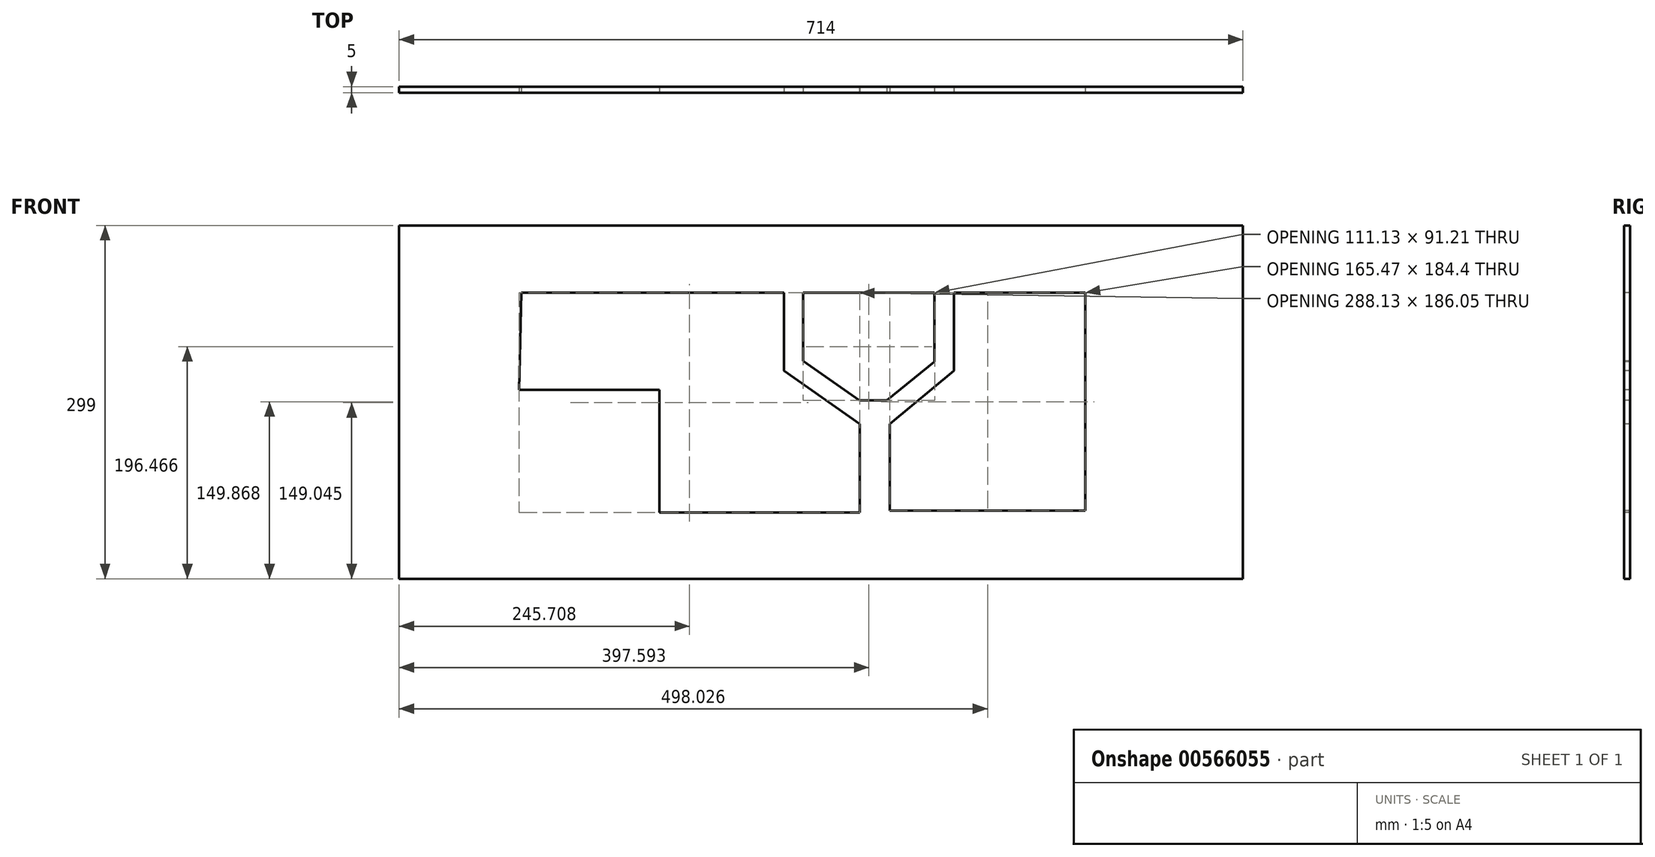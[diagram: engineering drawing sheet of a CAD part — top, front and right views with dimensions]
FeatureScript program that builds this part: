
annotation { "Feature Type Name" : "Feature", "Feature Type Description" : "" }
export const myFeature = defineFeature(function(context is Context, id is Id, definition is map)
    precondition{}
    {
        {
            var Q0;
            Q0=qCreatedBy(makeId("Top.planeOp"),FACE);
            var sketch = newSketch(context, id + "F0", { "sketchPlane" : qUnion([Q0])});
            skLineSegment(sketch, "E0.bottom", {"start": v(-666.68, 27.8) * mm, "end": v(47.32, 27.8) * mm});
            skLineSegment(sketch, "E0.top", {"start": v(-666.68, 22.8) * mm, "end": v(47.32, 22.8) * mm});
            skLineSegment(sketch, "E0.left", {"start": v(-666.68, 27.8) * mm, "end": v(-666.68, 22.8) * mm});
            skLineSegment(sketch, "E0.right", {"start": v(47.32, 27.8) * mm, "end": v(47.32, 22.8) * mm});
            skSolve(sketch);
        }
        {
            var Q0;
            Q0 = qSketchRegion(id + "F0", true);
            extrude(context, id + "F1", {"entities" : qUnion([Q0]), "depth" : 299 * mm, "offsetDistance" : 25 * mm});
        }
        {
            var Q0;
            Q0=makeQuery(id+"F1.opExtrude","SWEPT_FACE",FACE,{"disambiguationData":[OSD([sQuery(id+"F0.wireOp",EDGE,"E0.top")])]});
            var sketch = newSketch(context, id + "F2", { "sketchPlane" : qUnion([Q0])});
            skLineSegment(sketch, "E1", {"start": v(-563.39, 242.07) * mm, "end": v(-341.12, 242.07) * mm});
            skLineSegment(sketch, "E2", {"start": v(-341.12, 242.07) * mm, "end": v(-341.12, 176.21) * mm});
            skLineSegment(sketch, "E3", {"start": v(-341.12, 176.21) * mm, "end": v(-276.9, 130.93) * mm});
            skLineSegment(sketch, "E4", {"start": v(-276.9, 130.93) * mm, "end": v(-276.9, 56.02) * mm});
            skLineSegment(sketch, "E5", {"start": v(-276.9, 56.02) * mm, "end": v(-446.5, 56.02) * mm});
            skLineSegment(sketch, "E6", {"start": v(-446.5, 56.02) * mm, "end": v(-446.5, 159.75) * mm});
            skLineSegment(sketch, "E7", {"start": v(-446.5, 159.75) * mm, "end": v(-565.04, 159.75) * mm});
            skLineSegment(sketch, "E8", {"start": v(-565.04, 159.75) * mm, "end": v(-563.39, 242.07) * mm});
            skLineSegment(sketch, "E9", {"start": v(-324.65, 242.07) * mm, "end": v(-324.65, 184.44) * mm});
            skLineSegment(sketch, "E10", {"start": v(-324.65, 184.44) * mm, "end": v(-277.03, 150.86) * mm});
            skLineSegment(sketch, "E11", {"start": v(-277.03, 150.86) * mm, "end": v(-253.86, 150.86) * mm});
            skLineSegment(sketch, "E12", {"start": v(-253.86, 150.86) * mm, "end": v(-213.52, 183.62) * mm});
            skLineSegment(sketch, "E13", {"start": v(-213.52, 183.62) * mm, "end": v(-213.52, 242.07) * mm});
            skLineSegment(sketch, "E14", {"start": v(-213.52, 242.07) * mm, "end": v(-324.65, 242.07) * mm});
            skLineSegment(sketch, "E15", {"start": v(-197.06, 242.07) * mm, "end": v(-197.06, 176.21) * mm});
            skLineSegment(sketch, "E16", {"start": v(-197.06, 176.21) * mm, "end": v(-251.39, 130.93) * mm});
            skLineSegment(sketch, "E17", {"start": v(-251.39, 130.93) * mm, "end": v(-251.39, 57.67) * mm});
            skLineSegment(sketch, "E18", {"start": v(-251.39, 57.67) * mm, "end": v(-85.92, 57.67) * mm});
            skLineSegment(sketch, "E19", {"start": v(-85.92, 57.67) * mm, "end": v(-85.92, 242.07) * mm});
            skLineSegment(sketch, "E20", {"start": v(-85.92, 242.07) * mm, "end": v(-197.06, 242.07) * mm});
            skSolve(sketch);
        }
        {
            var Q0;
            Q0 = qSketchRegion(id + "F2", true);
            extrude(context, id + "F3", {"entities" : qUnion([Q0]), "operationType" : NewBodyOperationType.REMOVE, "oppositeDirection" : true, "depth" : 5 * mm, "offsetDistance" : 25 * mm});
        }
    });
